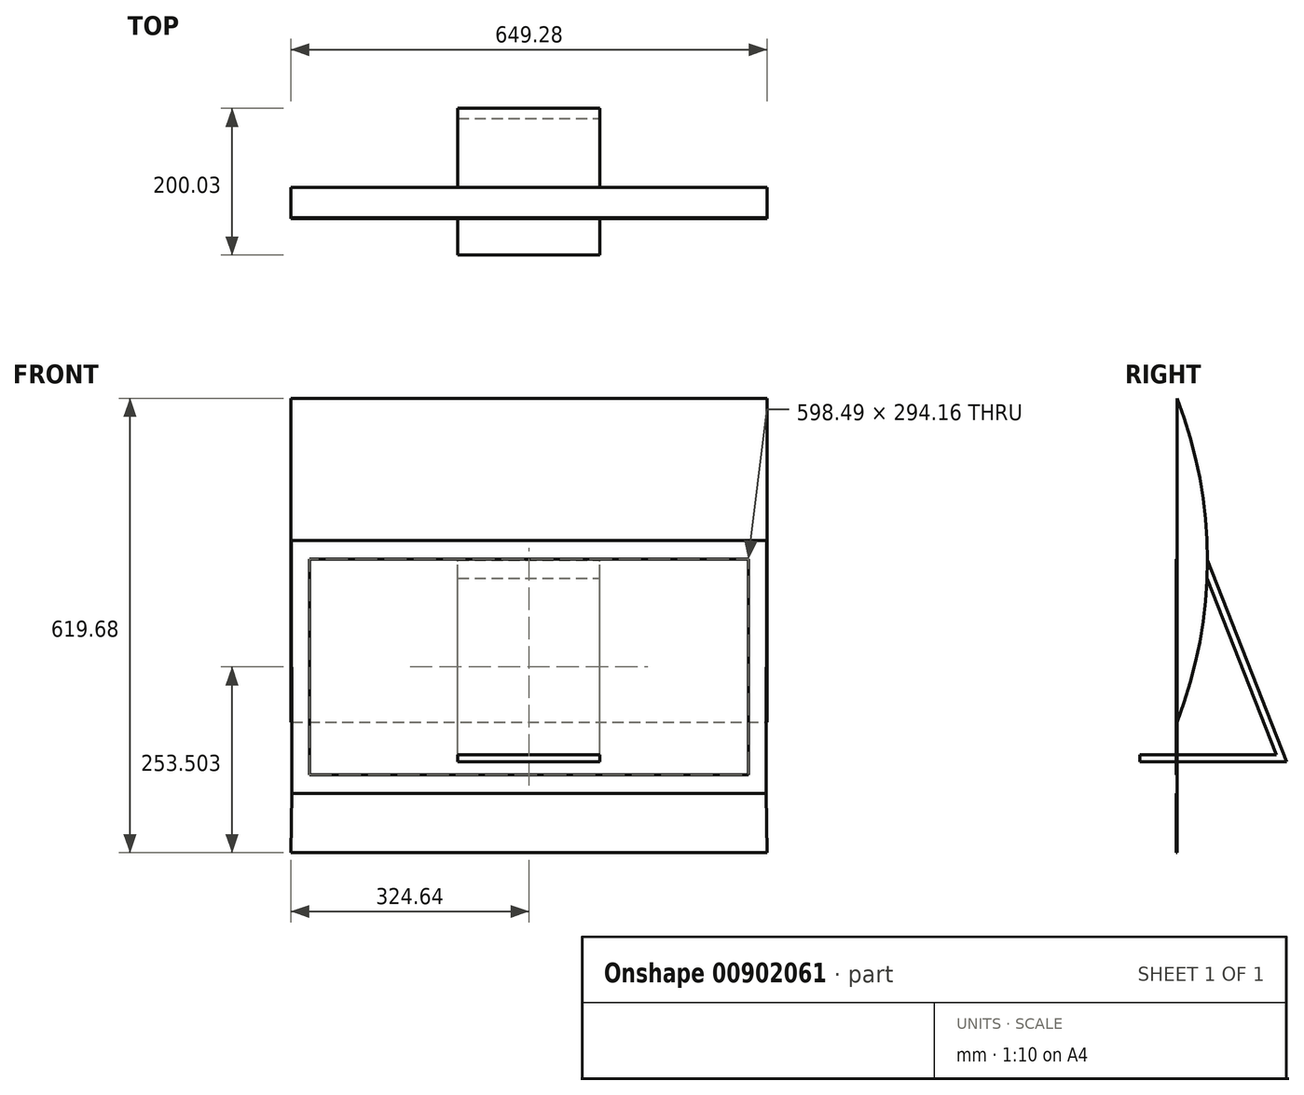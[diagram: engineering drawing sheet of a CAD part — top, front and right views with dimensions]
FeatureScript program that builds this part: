
annotation { "Feature Type Name" : "Feature", "Feature Type Description" : "" }
export const myFeature = defineFeature(function(context is Context, id is Id, definition is map)
    precondition{}
    {
        {
            var Q0;
            Q0=qCreatedBy(makeId("Right.planeOp"),FACE);
            var sketch = newSketch(context, id + "F0", { "sketchPlane" : qUnion([Q0])});
            skLineSegment(sketch, "E0", {"start": v(0, 0) * mm, "end": v(0, 441.32) * mm});
            skArc(sketch, "E1", {"start": v(0, 0) * mm, "mid": v(41.28, 220.66) * mm, "end": v(0, 441.32) * mm});
            skLineSegment(sketch, "E2", {"start": v(0, 0) * mm, "end": v(0, -53.98) * mm, "construction": true});
            skLineSegment(sketch, "E3", {"start": v(0, -53.98) * mm, "end": v(-50.8, -53.98) * mm});
            skLineSegment(sketch, "E4", {"start": v(0, -53.98) * mm, "end": v(149.23, -53.98) * mm});
            skLineSegment(sketch, "E5", {"start": v(149.23, -53.98) * mm, "end": v(41.28, 220.66) * mm});
            skPoint(sketch, "E5.endSnap0", {"position": v(41.28, 220.66) * mm});
            skLineSegment(sketch, "E6", {"start": v(-50.8, -53.98) * mm, "end": v(-50.8, -44.45) * mm});
            skLineSegment(sketch, "E7", {"start": v(-50.8, -44.45) * mm, "end": v(135.25, -44.45) * mm});
            skLineSegment(sketch, "E8", {"start": v(135.25, -44.45) * mm, "end": v(40.77, 195.9) * mm});
            skSolve(sketch);
        }
        {
            var Q0;
            {var subQ0=sQuery(id+"F0.wireOp",EDGE,"E0");Q0=makeQuery(id+"F0.imprint","IMPRINT",FACE,{"disambiguationData":[TD([[makeQuery(id+"F0.imprint","IMPRINT",EDGE,{"derivedFrom":subQ0}),-1.0]])]});}
            extrude(context, id + "F1", {"entities" : qUnion([Q0]), "oppositeDirection" : true, "depth" : 324.64 * mm, "offsetDistance" : 25.4 * mm, "hasSecondDirection" : true, "secondDirectionOppositeDirection" : false, "secondDirectionDepth" : 324.64 * mm});
        }
        {
            var Q0;
            Q0=makeQuery(id+"F0.imprint","IMPRINT",FACE,{"disambiguationData":[TD([[makeQuery(id+"F0.imprint","IMPRINT",EDGE,{"derivedFrom":sQuery(id+"F0.wireOp",EDGE,"E3")}),-1.0]])]});
            extrude(context, id + "F2", {"entities" : qUnion([Q0]), "operationType" : NewBodyOperationType.ADD, "surfaceOperationType" : NewSurfaceOperationType.ADD, "oppositeDirection" : true, "depth" : 96.84 * mm, "offsetDistance" : 25.4 * mm, "hasSecondDirection" : true, "secondDirectionOppositeDirection" : false, "secondDirectionDepth" : 96.84 * mm});
        }
        {
            var Q0;
            Q0=qCreatedBy(makeId("Front.planeOp"),FACE);
            var sketch = newSketch(context, id + "F3", { "sketchPlane" : qUnion([Q0])});
            skLineSegment(sketch, "E9.bottom", {"start": v(-299.24, 222.23) * mm, "end": v(299.24, 222.23) * mm});
            skLineSegment(sketch, "E9.top", {"start": v(-299.24, -71.93) * mm, "end": v(299.24, -71.93) * mm});
            skLineSegment(sketch, "E9.left", {"start": v(-299.24, 222.23) * mm, "end": v(-299.24, -71.93) * mm});
            skLineSegment(sketch, "E9.right", {"start": v(299.24, 222.23) * mm, "end": v(299.24, -71.93) * mm});
            skLineSegment(sketch, "E10", {"start": v(-323.12, -97.33) * mm, "end": v(323.12, -97.33) * mm});
            skLineSegment(sketch, "E11", {"start": v(-323.12, -97.33) * mm, "end": v(-323.87, 247.63) * mm});
            skLineSegment(sketch, "E12", {"start": v(-323.87, 247.63) * mm, "end": v(323.9, 247.63) * mm});
            skLineSegment(sketch, "E13", {"start": v(323.9, 247.63) * mm, "end": v(323.12, -97.33) * mm});
            skLineSegment(sketch, "E14", {"start": v(323.12, -97.33) * mm, "end": v(324.64, -178.35) * mm});
            skLineSegment(sketch, "E15", {"start": v(324.64, -178.35) * mm, "end": v(-324.64, -178.35) * mm});
            skLineSegment(sketch, "E16", {"start": v(-324.64, -178.35) * mm, "end": v(-323.12, -97.33) * mm});
            skPoint(sketch, "E17", {"position": v(0, -117.6) * mm});
            skPoint(sketch, "E18", {"position": v(0, -158.09) * mm});
            skPoint(sketch, "E19", {"position": v(0, -178.35) * mm});
            skPoint(sketch, "E20", {"position": v(323.88, -137.84) * mm});
            skPoint(sketch, "E21", {"position": v(-323.88, -137.84) * mm});
            skPoint(sketch, "E22", {"position": v(0, -97.33) * mm});
            skPoint(sketch, "E23", {"position": v(0, -71.93) * mm});
            skPoint(sketch, "E24", {"position": v(15.64, -137.84) * mm});
            skPoint(sketch, "E25", {"position": v(-15.64, -137.84) * mm});
            skPoint(sketch, "E26", {"position": v(0, 441.45) * mm});
            skPoint(sketch, "E27", {"position": v(0, 247.63) * mm});
            skSolve(sketch);
        }
        {
            var Q0;
            Q0=makeQuery(id+"F3.imprint","IMPRINT",FACE,{"disambiguationData":[TD([[makeQuery(id+"F3.imprint","IMPRINT",EDGE,{"derivedFrom":sQuery(id+"F3.wireOp",EDGE,"E9.bottom")}),1.0]])]});
            extrude(context, id + "F4", {"entities" : qUnion([Q0]), "surfaceOperationType" : NewSurfaceOperationType.ADD, "depth" : .1 * mm, "offsetDistance" : 25.4 * mm});
        }
        {
            var Q0;
            Q0=makeQuery(id+"F3.imprint","IMPRINT",FACE,{"disambiguationData":[TD([[makeQuery(id+"F3.imprint","IMPRINT",EDGE,{"derivedFrom":sQuery(id+"F3.wireOp",EDGE,"E10")}),-1.0]])]});
            extrude(context, id + "F5", {"entities" : qUnion([Q0]), "depth" : 1 * mm, "offsetDistance" : 25.4 * mm});
        }
        {
            var Q0;
            Q0=makeQuery(id+"F3.imprint","IMPRINT",FACE,{"disambiguationData":[TD([[makeQuery(id+"F3.imprint","IMPRINT",EDGE,{"derivedFrom":sQuery(id+"F3.wireOp",EDGE,"E9.bottom")}),-1.0]])]});
            extrude(context, id + "F6", {"entities" : qUnion([Q0]), "depth" : 1 * mm, "offsetDistance" : 25.4 * mm});
        }
    });
